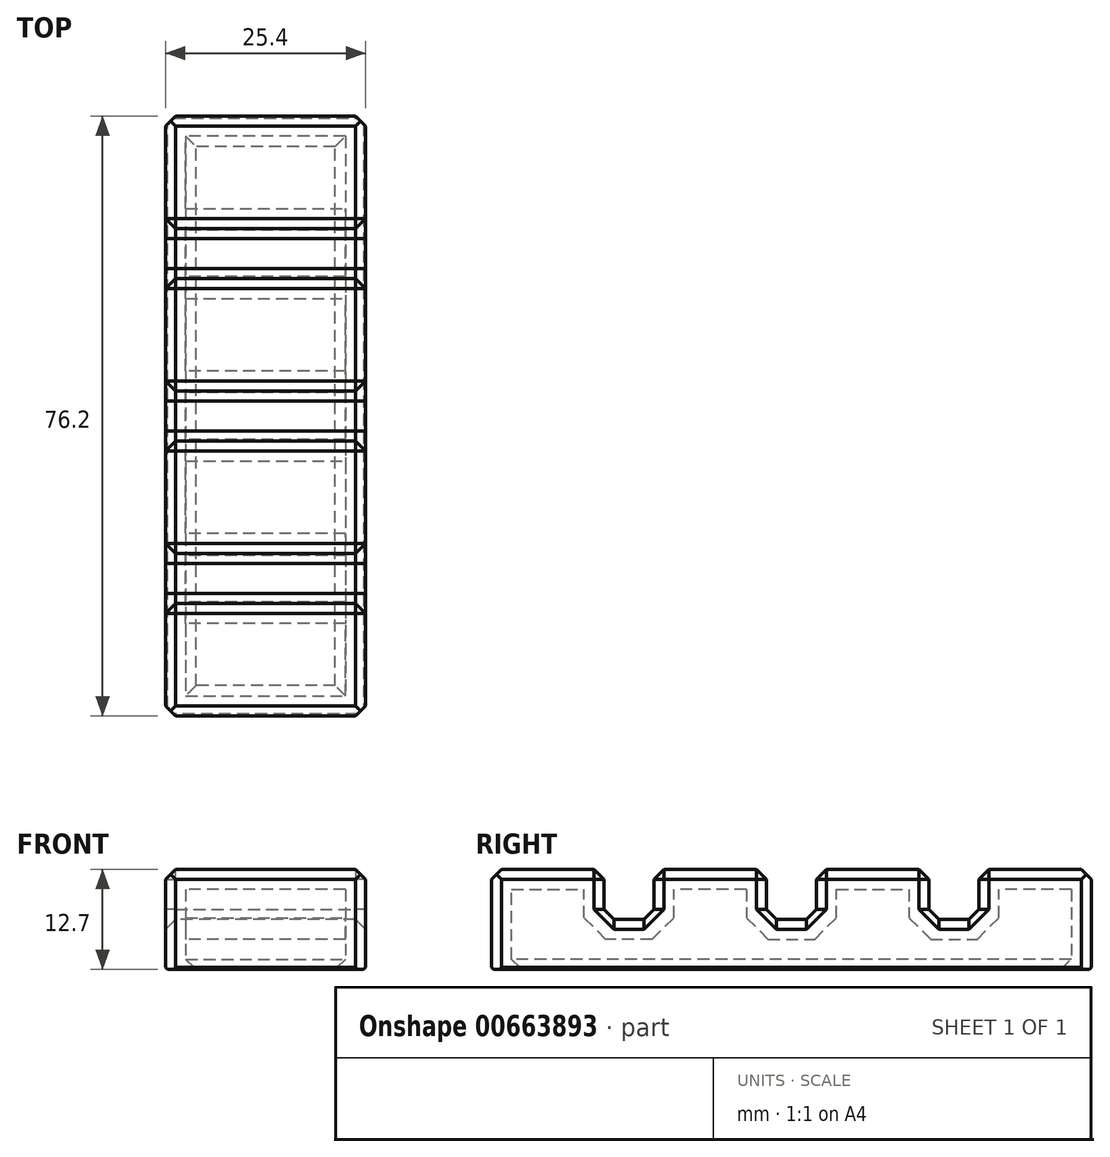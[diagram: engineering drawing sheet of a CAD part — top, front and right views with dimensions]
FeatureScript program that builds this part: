
annotation { "Feature Type Name" : "Feature", "Feature Type Description" : "" }
export const myFeature = defineFeature(function(context is Context, id is Id, definition is map)
    precondition{}
    {
        {
            var Q0;
            Q0=qCreatedBy(makeId("Top.planeOp"),FACE);
            var sketch = newSketch(context, id + "F0", { "sketchPlane" : qUnion([Q0])});
            skLineSegment(sketch, "E0.bottom", {"start": v(12.7, -38.1) * mm, "end": v(-12.7, -38.1) * mm});
            skLineSegment(sketch, "E0.top", {"start": v(12.7, 38.1) * mm, "end": v(-12.7, 38.1) * mm});
            skLineSegment(sketch, "E0.left", {"start": v(12.7, -38.1) * mm, "end": v(12.7, 38.1) * mm});
            skLineSegment(sketch, "E0.right", {"start": v(-12.7, -38.1) * mm, "end": v(-12.7, 38.1) * mm});
            skPoint(sketch, "E0.middle", {"position": v(0, 0) * mm});
            skSolve(sketch);
        }
        {
            var Q0;
            Q0=makeQuery(id+"F0.imprint","IMPRINT",FACE,{"disambiguationData":[TD([[makeQuery(id+"F0.imprint","IMPRINT",EDGE,{"derivedFrom":sQuery(id+"F0.wireOp",EDGE,"E0.bottom")}),-1.0]])]});
            extrude(context, id + "F1", {"entities" : qUnion([Q0]), "depth" : 12.7 * mm, "offsetDistance" : 25.4 * mm});
        }
        {
            var Q0;
            Q0=makeQuery(id+"F1.opExtrude","SWEPT_FACE",FACE,{"disambiguationData":[OSD([sQuery(id+"F0.wireOp",EDGE,"E0.left")])]});
            var sketch = newSketch(context, id + "F2", { "sketchPlane" : qUnion([Q0])});
            skPoint(sketch, "E1.middle", {"position": v(0, 12.7) * mm});
            skLineSegment(sketch, "E2", {"start": v(-38.1, 6.35) * mm, "end": v(38.1, 6.35) * mm, "construction": true});
            skLineSegment(sketch, "E3.bottom", {"start": v(3.18, 6.35) * mm, "end": v(-3.17, 6.35) * mm});
            skLineSegment(sketch, "E3.top", {"start": v(3.18, 19.05) * mm, "end": v(-3.17, 19.05) * mm});
            skLineSegment(sketch, "E3.left", {"start": v(3.18, 6.35) * mm, "end": v(3.18, 19.05) * mm});
            skLineSegment(sketch, "E3.right", {"start": v(-3.17, 6.35) * mm, "end": v(-3.17, 19.05) * mm});
            skLineSegment(sketch, "E4.bottom", {"start": v(23.83, 6.35) * mm, "end": v(17.48, 6.35) * mm});
            skLineSegment(sketch, "E4.top", {"start": v(23.83, 19.05) * mm, "end": v(17.48, 19.05) * mm});
            skLineSegment(sketch, "E4.left", {"start": v(23.83, 6.35) * mm, "end": v(23.83, 19.05) * mm});
            skLineSegment(sketch, "E4.right", {"start": v(17.48, 6.35) * mm, "end": v(17.48, 19.05) * mm});
            skPoint(sketch, "E4.middle", {"position": v(20.65, 12.7) * mm});
            skLineSegment(sketch, "E5.bottom", {"start": v(-17.48, 6.35) * mm, "end": v(-23.83, 6.35) * mm});
            skLineSegment(sketch, "E5.top", {"start": v(-17.48, 19.05) * mm, "end": v(-23.83, 19.05) * mm});
            skLineSegment(sketch, "E5.left", {"start": v(-17.48, 6.35) * mm, "end": v(-17.48, 19.05) * mm});
            skLineSegment(sketch, "E5.right", {"start": v(-23.83, 6.35) * mm, "end": v(-23.83, 19.05) * mm});
            skPoint(sketch, "E5.middle", {"position": v(-20.65, 12.7) * mm});
            skSolve(sketch);
        }
        {
            var Q0;
            Q0 = qSketchRegion(id + "F2", true);
            extrude(context, id + "F3", {"entities" : qUnion([Q0]), "operationType" : NewBodyOperationType.REMOVE, "endBound" : BoundingType.THROUGH_ALL, "oppositeDirection" : true, "depth" : 25.4 * mm, "offsetDistance" : 25.4 * mm});
        }
        {
            var Q0;
            {var subQ0=sQuery(id+"F0.wireOp",EDGE,"E0.left");var subQ1=sQuery(id+"F0.wireOp",EDGE,"E0.right");Q0=makeQuery(id+"F3.boolean.opBoolean","SPLIT",FACE,{"disambiguationData":[TD([makeQuery(id+"F3.opExtrude","SWEPT_FACE",FACE,{"disambiguationData":[OSD([sQuery(id+"F2.wireOp",EDGE,"E3.right")])]})])],"derivedFrom":makeQuery(id+"F1.opExtrude","CAP_FACE",FACE,{"disambiguationData":[OSD([sQuery(id+"F0.wireOp",EDGE,"E0.bottom"),sQuery(id+"F0.wireOp",EDGE,"E0.top"),subQ0,subQ1])],"isStart":false})});}
            var Q1;
            {var subQ0=sQuery(id+"F0.wireOp",EDGE,"E0.bottom");var subQ1=sQuery(id+"F0.wireOp",EDGE,"E0.right");var subQ2=sQuery(id+"F0.wireOp",EDGE,"E0.left");Q1=makeQuery(id+"F3.boolean.opBoolean","SPLIT",FACE,{"disambiguationData":[TD([makeQuery(id+"F1.opExtrude","SWEPT_FACE",FACE,{"disambiguationData":[OSD([subQ0])]})])],"derivedFrom":makeQuery(id+"F1.opExtrude","CAP_FACE",FACE,{"disambiguationData":[OSD([subQ0,sQuery(id+"F0.wireOp",EDGE,"E0.top"),subQ2,subQ1])],"isStart":false})});}
            var Q2;
            {var subQ0=sQuery(id+"F0.wireOp",EDGE,"E0.left");var subQ1=sQuery(id+"F0.wireOp",EDGE,"E0.right");Q2=makeQuery(id+"F3.boolean.opBoolean","SPLIT",FACE,{"disambiguationData":[TD([makeQuery(id+"F3.opExtrude","SWEPT_FACE",FACE,{"disambiguationData":[OSD([sQuery(id+"F2.wireOp",EDGE,"E3.left")])]})])],"derivedFrom":makeQuery(id+"F1.opExtrude","CAP_FACE",FACE,{"disambiguationData":[OSD([sQuery(id+"F0.wireOp",EDGE,"E0.bottom"),sQuery(id+"F0.wireOp",EDGE,"E0.top"),subQ0,subQ1])],"isStart":false})});}
            var Q3;
            {var subQ0=sQuery(id+"F0.wireOp",EDGE,"E0.top");var subQ1=sQuery(id+"F0.wireOp",EDGE,"E0.left");var subQ2=sQuery(id+"F0.wireOp",EDGE,"E0.right");Q3=makeQuery(id+"F3.boolean.opBoolean","SPLIT",FACE,{"disambiguationData":[TD([makeQuery(id+"F1.opExtrude","SWEPT_FACE",FACE,{"disambiguationData":[OSD([subQ0])]})])],"derivedFrom":makeQuery(id+"F1.opExtrude","CAP_FACE",FACE,{"disambiguationData":[OSD([sQuery(id+"F0.wireOp",EDGE,"E0.bottom"),subQ0,subQ1,subQ2])],"isStart":false})});}
            var Q4;
            Q4=makeQuery(id+"F3.boolean.opBoolean","COPY",FACE,{"derivedFrom":makeQuery(id+"F3.opExtrude","SWEPT_FACE",FACE,{"disambiguationData":[OSD([sQuery(id+"F2.wireOp",EDGE,"E5.bottom")])]})});
            var Q5;
            Q5=makeQuery(id+"F3.boolean.opBoolean","COPY",FACE,{"derivedFrom":makeQuery(id+"F3.opExtrude","SWEPT_FACE",FACE,{"disambiguationData":[OSD([sQuery(id+"F2.wireOp",EDGE,"E3.bottom")])]})});
            var Q6;
            Q6=makeQuery(id+"F3.boolean.opBoolean","COPY",EDGE,{"derivedFrom":makeQuery(id+"F3.opExtrude","CAP_EDGE",EDGE,{"disambiguationData":[OSD([sQuery(id+"F2.wireOp",EDGE,"E4.right")])],"isStart":true})});
            var Q7;
            Q7=makeQuery(id+"F3.boolean.opBoolean","COPY",FACE,{"derivedFrom":makeQuery(id+"F3.opExtrude","SWEPT_FACE",FACE,{"disambiguationData":[OSD([sQuery(id+"F2.wireOp",EDGE,"E4.bottom")])]})});
            chamfer(context, id + "F4", {"entities" : qUnion([Q0, Q1, Q2, Q3, Q4, Q5, Q6, Q7]), "width" : 1.27 * mm, "tangentPropagation" : true});
        }
        {
            var Q0;
            Q0=makeQuery(id+"F1.opExtrude","SWEPT_EDGE",EDGE,{"disambiguationData":[OSD([sQuery(id+"F0.wireOp",EDGE,"E0.bottom"),sQuery(id+"F0.wireOp",EDGE,"E0.right")])]});
            var Q1;
            Q1=makeQuery(id+"F1.opExtrude","SWEPT_EDGE",EDGE,{"disambiguationData":[OSD([sQuery(id+"F0.wireOp",EDGE,"E0.top"),sQuery(id+"F0.wireOp",EDGE,"E0.right")])]});
            var Q2;
            Q2=makeQuery(id+"F1.opExtrude","SWEPT_EDGE",EDGE,{"disambiguationData":[OSD([sQuery(id+"F0.wireOp",EDGE,"E0.top"),sQuery(id+"F0.wireOp",EDGE,"E0.left")])]});
            var Q3;
            Q3=makeQuery(id+"F1.opExtrude","SWEPT_EDGE",EDGE,{"disambiguationData":[OSD([sQuery(id+"F0.wireOp",EDGE,"E0.bottom"),sQuery(id+"F0.wireOp",EDGE,"E0.left")])]});
            chamfer(context, id + "F5", {"entities" : qUnion([Q0, Q1, Q2, Q3]), "width" : 1.27 * mm, "tangentPropagation" : true});
        }
        {
            var Q0;
            Q0=makeQuery(id+"F1.opExtrude","CAP_EDGE",EDGE,{"disambiguationData":[OSD([sQuery(id+"F0.wireOp",EDGE,"E0.left")])],"isStart":true});
            var Q1;
            Q1=makeQuery(id+"F1.opExtrude","CAP_EDGE",EDGE,{"disambiguationData":[OSD([sQuery(id+"F0.wireOp",EDGE,"E0.right")])],"isStart":true});
            var Q2;
            Q2=makeQuery(id+"F1.opExtrude","CAP_EDGE",EDGE,{"disambiguationData":[OSD([sQuery(id+"F0.wireOp",EDGE,"E0.top")])],"isStart":true});
            var Q3;
            Q3=makeQuery(id+"F1.opExtrude","CAP_EDGE",EDGE,{"disambiguationData":[OSD([sQuery(id+"F0.wireOp",EDGE,"E0.bottom")])],"isStart":true});
            chamfer(context, id + "F6", {"entities" : qUnion([Q0, Q1, Q2, Q3]), "width" : 0.25 * mm, "tangentPropagation" : true});
        }
        {
            var Q0;
            Q0=makeQuery(id+"F1.opExtrude","CAP_FACE",FACE,{"disambiguationData":[OSD([sQuery(id+"F0.wireOp",EDGE,"E0.bottom"),sQuery(id+"F0.wireOp",EDGE,"E0.top"),sQuery(id+"F0.wireOp",EDGE,"E0.left"),sQuery(id+"F0.wireOp",EDGE,"E0.right")])],"isStart":true});
            shell(context, id + "F7", {"entities" : qUnion([Q0]), "thickness" : 2.54 * mm});
        }
    });
